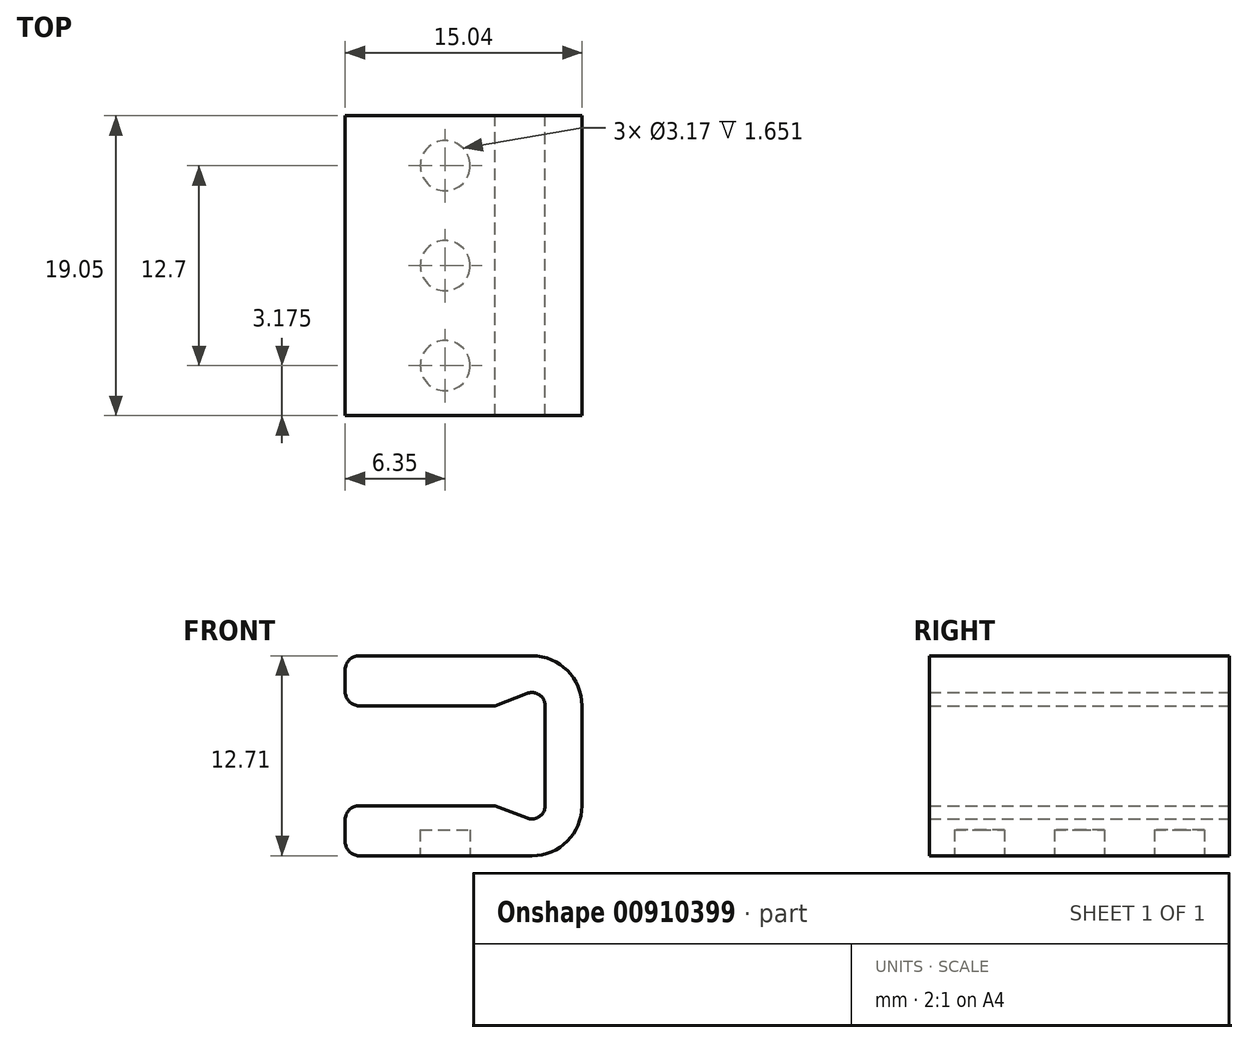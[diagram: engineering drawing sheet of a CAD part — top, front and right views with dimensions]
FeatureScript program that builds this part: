
annotation { "Feature Type Name" : "Feature", "Feature Type Description" : "" }
export const myFeature = defineFeature(function(context is Context, id is Id, definition is map)
    precondition{}
    {
        {
            var Q0;
            Q0=qCreatedBy(makeId("Front.planeOp"),FACE);
            var sketch = newSketch(context, id + "F0", { "sketchPlane" : qUnion([Q0])});
            skLineSegment(sketch, "E0", {"start": v(0, 0) * mm, "end": v(0, 6.35) * mm});
            skLineSegment(sketch, "E1", {"start": v(-11.81, 6.35) * mm, "end": v(-3.18, 6.35) * mm});
            skLineSegment(sketch, "E2", {"start": v(-12.7, 7.24) * mm, "end": v(-12.7, 8.64) * mm});
            skLineSegment(sketch, "E3", {"start": v(-11.81, 9.53) * mm, "end": v(-0.84, 9.53) * mm});
            skLineSegment(sketch, "E4", {"start": v(-0.84, -3.17) * mm, "end": v(-11.81, -3.17) * mm});
            skLineSegment(sketch, "E5", {"start": v(-12.7, -2.29) * mm, "end": v(-12.7, -0.89) * mm});
            skLineSegment(sketch, "E6", {"start": v(-11.81, 0) * mm, "end": v(-3.18, 0) * mm});
            skArc(sketch, "E7", {"start": v(0, 6.35) * mm, "mid": v(-0.36, 7.04) * mm, "end": v(-1.14, 7.13) * mm});
            skArc(sketch, "E8", {"start": v(0, 0) * mm, "mid": v(-0.36, -0.7) * mm, "end": v(-1.14, -0.78) * mm});
            skLineSegment(sketch, "E9", {"start": v(-1.14, 7.13) * mm, "end": v(-3.18, 6.35) * mm});
            skLineSegment(sketch, "E10", {"start": v(-1.14, -0.78) * mm, "end": v(-3.18, 0) * mm});
            skArc(sketch, "E11", {"start": v(-0.84, 9.53) * mm, "mid": v(1.4, 8.6) * mm, "end": v(2.34, 6.35) * mm});
            skArc(sketch, "E12", {"start": v(-0.84, -3.17) * mm, "mid": v(1.4, -2.25) * mm, "end": v(2.34, 0) * mm});
            skLineSegment(sketch, "E13", {"start": v(2.34, 6.35) * mm, "end": v(2.34, 0) * mm});
            skPoint(sketch, "E14.visualSharp", {"position": v(-12.7, 9.53) * mm});
            skArc(sketch, "E14.filletArc", {"start": v(-11.81, 9.53) * mm, "mid": v(-12.44, 9.26) * mm, "end": v(-12.7, 8.64) * mm});
            skPoint(sketch, "E15.visualSharp", {"position": v(-12.7, -3.18) * mm});
            skArc(sketch, "E15.filletArc", {"start": v(-12.7, -2.29) * mm, "mid": v(-12.44, -2.91) * mm, "end": v(-11.81, -3.18) * mm});
            skPoint(sketch, "E16.visualSharp", {"position": v(-12.7, 6.35) * mm});
            skArc(sketch, "E16.filletArc", {"start": v(-12.7, 7.24) * mm, "mid": v(-12.44, 6.61) * mm, "end": v(-11.81, 6.35) * mm});
            skPoint(sketch, "E17.visualSharp", {"position": v(-12.7, 0) * mm});
            skArc(sketch, "E17.filletArc", {"start": v(-11.81, 0) * mm, "mid": v(-12.44, -0.26) * mm, "end": v(-12.7, -0.89) * mm});
            skSolve(sketch);
        }
        {
            var Q0;
            Q0=qSketchRegion(id+"F0",true);
            extrude(context, id + "F1", {"entities" : qUnion([Q0]), "depth" : 19.05 * mm, "offsetDistance" : 25.4 * mm});
        }
        {
            var Q0;
            Q0=makeQuery(id+"F1.opExtrude","SWEPT_FACE",FACE,{"disambiguationData":[OSD([sQuery(id+"F0.wireOp",EDGE,"E4")])]});
            var sketch = newSketch(context, id + "F2", { "sketchPlane" : qUnion([Q0])});
            skCircle(sketch, "E18", {"center": v(-6.35, 15.88) * mm, "radius": 1.59 * mm});
            skCircle(sketch, "E19", {"center": v(-6.35, 3.18) * mm, "radius": 1.59 * mm});
            skCircle(sketch, "E20", {"center": v(-6.35, 9.53) * mm, "radius": 1.59 * mm});
            skLineSegment(sketch, "E21", {"start": v(-11.81, 9.53) * mm, "end": v(-6.35, 9.53) * mm, "construction": true});
            skLineSegment(sketch, "E22", {"start": v(-6.35, 15.88) * mm, "end": v(-6.35, 9.53) * mm, "construction": true});
            skLineSegment(sketch, "E23", {"start": v(-6.35, 3.18) * mm, "end": v(-6.35, 9.53) * mm, "construction": true});
            skSolve(sketch);
        }
        {
            var Q0;
            Q0=qSketchRegion(id+"F2",true);
            extrude(context, id + "F3", {"entities" : qUnion([Q0]), "operationType" : NewBodyOperationType.REMOVE, "oppositeDirection" : true, "depth" : 1.65 * mm, "offsetDistance" : 25.4 * mm});
        }
    });
